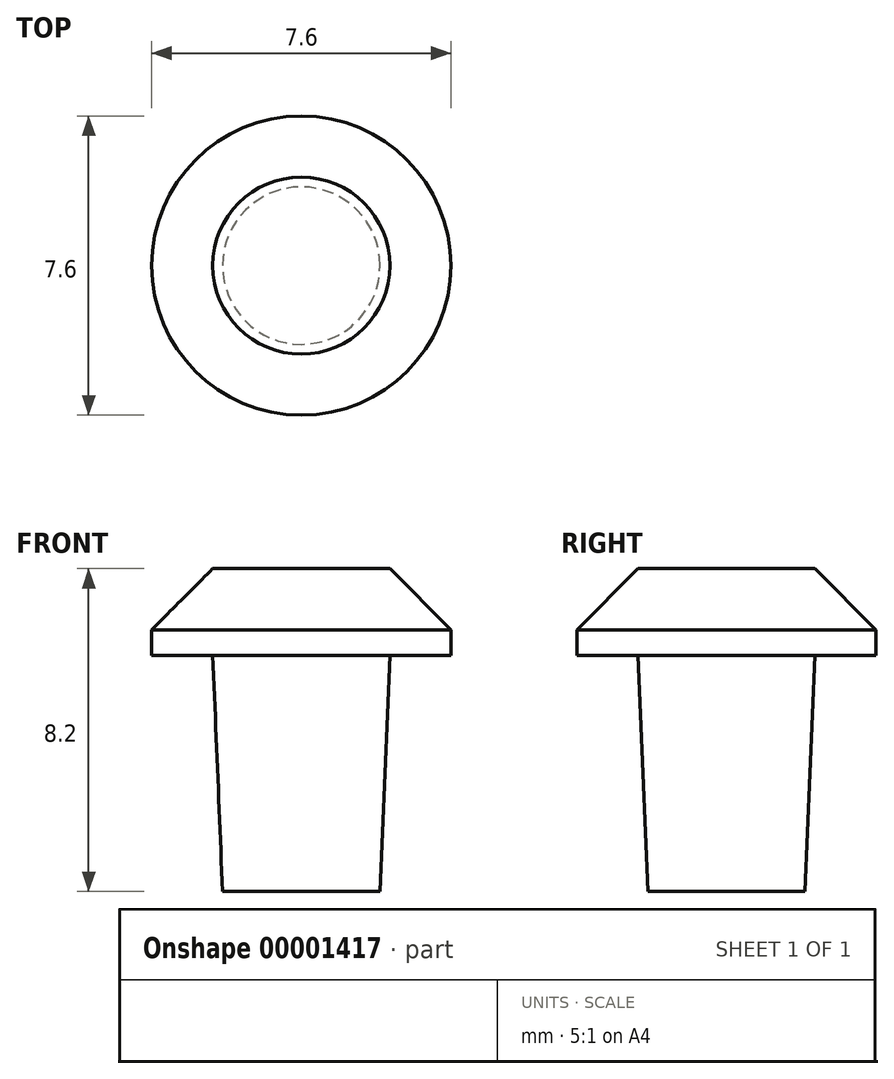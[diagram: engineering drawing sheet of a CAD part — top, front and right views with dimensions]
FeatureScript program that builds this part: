
annotation { "Feature Type Name" : "Feature", "Feature Type Description" : "" }
export const myFeature = defineFeature(function(context is Context, id is Id, definition is map)
    precondition{}
    {
        {
            var Q0;
            Q0=qCreatedBy(makeId("Front.planeOp"),FACE);
            var sketch = newSketch(context, id + "F0", { "sketchPlane" : qUnion([Q0])});
            skLineSegment(sketch, "E0", {"start": v(0, 0) * mm, "end": v(0, 2.2) * mm});
            skLineSegment(sketch, "E1", {"start": v(0, 2.2) * mm, "end": v(2.25, 2.2) * mm});
            skLineSegment(sketch, "E2", {"start": v(3.8, 0) * mm, "end": v(2.25, 0) * mm});
            skLineSegment(sketch, "E3", {"start": v(2.25, 0) * mm, "end": v(2, -6) * mm});
            skLineSegment(sketch, "E4", {"start": v(2, -6) * mm, "end": v(0, -6) * mm});
            skLineSegment(sketch, "E5", {"start": v(0, -6) * mm, "end": v(0, 0) * mm});
            skLineSegment(sketch, "E6", {"start": v(0, -6) * mm, "end": v(0, -9.46) * mm, "construction": true});
            skLineSegment(sketch, "E7", {"start": v(0, 2.2) * mm, "end": v(0, 4.23) * mm, "construction": true});
            skLineSegment(sketch, "E8", {"start": v(3.8, 0) * mm, "end": v(3.8, 0.65) * mm});
            skLineSegment(sketch, "E9", {"start": v(3.8, 0.65) * mm, "end": v(2.25, 2.2) * mm});
            skSolve(sketch);
        }
        {
            var Q0;
            Q0 = qSketchRegion(id + "F0", true);
            var Q1;
            Q1=sQuery(id+"F0.wireOp",EDGE,"E7");
            revolve(context, id + "F1", {"surfaceOperationType" : NewSurfaceOperationType.NEW, "entities" : qUnion([Q0]), "axis" : qUnion([Q1]), "revolveType" : RevolveType.FULL});
        }
    });
